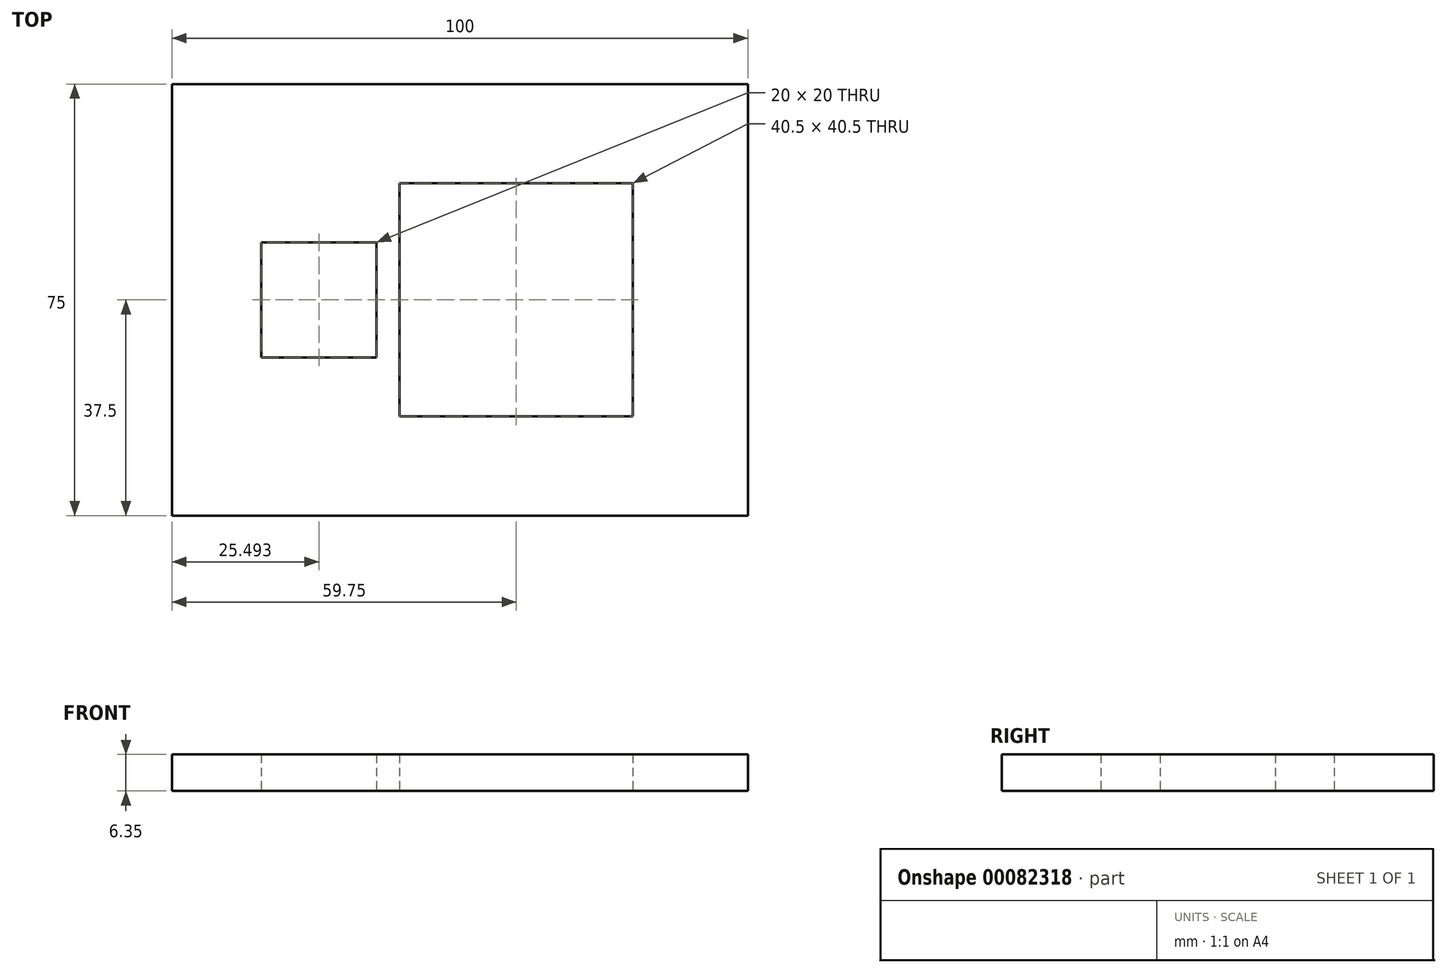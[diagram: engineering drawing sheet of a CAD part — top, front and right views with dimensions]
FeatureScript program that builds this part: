
annotation { "Feature Type Name" : "Feature", "Feature Type Description" : "" }
export const myFeature = defineFeature(function(context is Context, id is Id, definition is map)
    precondition{}
    {
        {
            var Q0;
            Q0=qCreatedBy(makeId("Top.planeOp"),FACE);
            var sketch = newSketch(context, id + "F0", { "sketchPlane" : qUnion([Q0])});
            skLineSegment(sketch, "E0.bottom", {"start": v(50, -37.5) * mm, "end": v(-50, -37.5) * mm});
            skLineSegment(sketch, "E0.top", {"start": v(50, 37.5) * mm, "end": v(-50, 37.5) * mm});
            skLineSegment(sketch, "E0.left", {"start": v(50, -37.5) * mm, "end": v(50, 37.5) * mm});
            skLineSegment(sketch, "E0.right", {"start": v(-50, -37.5) * mm, "end": v(-50, 37.5) * mm});
            skPoint(sketch, "E0.middle", {"position": v(0, 0) * mm});
            skLineSegment(sketch, "E1.bottom", {"start": v(-34.5, 10) * mm, "end": v(-14.5, 10) * mm});
            skLineSegment(sketch, "E1.top", {"start": v(-34.5, -10) * mm, "end": v(-14.5, -10) * mm});
            skLineSegment(sketch, "E1.left", {"start": v(-34.5, 10) * mm, "end": v(-34.5, -10) * mm});
            skLineSegment(sketch, "E1.right", {"start": v(-14.5, 10) * mm, "end": v(-14.5, -10) * mm});
            skLineSegment(sketch, "E2.bottom", {"start": v(30, -20.25) * mm, "end": v(-10.5, -20.25) * mm});
            skLineSegment(sketch, "E2.top", {"start": v(30, 20.25) * mm, "end": v(-10.5, 20.25) * mm});
            skLineSegment(sketch, "E2.left", {"start": v(30, -20.25) * mm, "end": v(30, 20.25) * mm});
            skLineSegment(sketch, "E2.right", {"start": v(-10.5, -20.25) * mm, "end": v(-10.5, 20.25) * mm});
            skPoint(sketch, "E2.middle", {"position": v(9.75, 0) * mm});
            skLineSegment(sketch, "E3", {"start": v(30, -20.25) * mm, "end": v(50, -20.25) * mm});
            skLineSegment(sketch, "E4", {"start": v(-14.5, -10) * mm, "end": v(0, 0) * mm, "construction": true});
            skLineSegment(sketch, "E5", {"start": v(-14.5, 10) * mm, "end": v(0, 0) * mm, "construction": true});
            skLineSegment(sketch, "E6.bottom", {"start": v(-56.35, 43.85) * mm, "end": v(56.35, 43.85) * mm});
            skLineSegment(sketch, "E6.top", {"start": v(-56.35, -43.85) * mm, "end": v(56.35, -43.85) * mm});
            skLineSegment(sketch, "E6.left", {"start": v(-56.35, 43.85) * mm, "end": v(-56.35, -43.85) * mm});
            skLineSegment(sketch, "E6.right", {"start": v(56.35, 43.85) * mm, "end": v(56.35, -43.85) * mm});
            skLineSegment(sketch, "E7", {"start": v(-50, 37.5) * mm, "end": v(-50, 43.85) * mm});
            skLineSegment(sketch, "E8", {"start": v(-50, 37.5) * mm, "end": v(-56.35, 37.5) * mm});
            skLineSegment(sketch, "E9", {"start": v(50, -37.5) * mm, "end": v(56.35, -37.5) * mm});
            skLineSegment(sketch, "E10", {"start": v(50, -37.5) * mm, "end": v(50, -43.85) * mm});
            skSolve(sketch);
        }
        {
            var Q0;
            Q0=makeQuery(id+"F0.imprint","IMPRINT",FACE,{"disambiguationData":[TD([[makeQuery(id+"F0.imprint","IMPRINT",EDGE,{"derivedFrom":sQuery(id+"F0.wireOp",EDGE,"E0.bottom")}),-1.0]])]});
            extrude(context, id + "F1", {"entities" : qUnion([Q0]), "depth" : 6.35 * mm});
        }
    });
